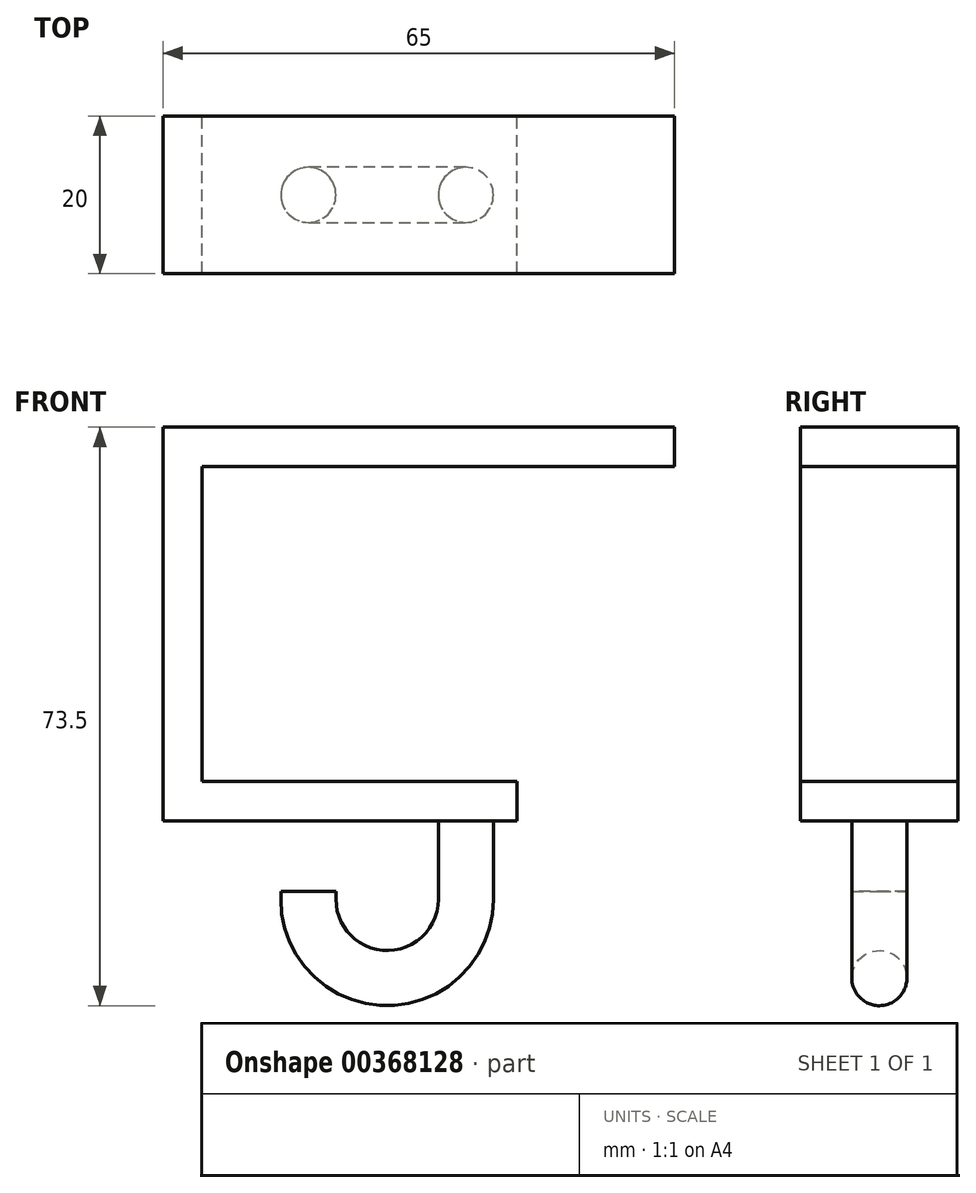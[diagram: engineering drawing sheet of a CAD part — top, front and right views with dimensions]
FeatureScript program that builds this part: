
annotation { "Feature Type Name" : "Feature", "Feature Type Description" : "" }
export const myFeature = defineFeature(function(context is Context, id is Id, definition is map)
    precondition{}
    {
        {
            var Q0;
            Q0=qCreatedBy(makeId("Front.planeOp"),FACE);
            var sketch = newSketch(context, id + "F0", { "sketchPlane" : qUnion([Q0])});
            skLineSegment(sketch, "E0", {"start": v(0, 0) * mm, "end": v(0, -40) * mm});
            skLineSegment(sketch, "E1", {"start": v(0, -40) * mm, "end": v(40, -40) * mm});
            skLineSegment(sketch, "E2", {"start": v(0, 0) * mm, "end": v(60, 0) * mm});
            skLineSegment(sketch, "E3", {"start": v(60, 0) * mm, "end": v(60, 5) * mm});
            skLineSegment(sketch, "E4", {"start": v(60, 5) * mm, "end": v(-5, 5) * mm});
            skLineSegment(sketch, "E5", {"start": v(-5, 5) * mm, "end": v(-5, -45) * mm});
            skLineSegment(sketch, "E6", {"start": v(-5, -45) * mm, "end": v(40, -45) * mm});
            skLineSegment(sketch, "E7", {"start": v(40, -45) * mm, "end": v(40, -40) * mm});
            skSolve(sketch);
        }
        {
            var Q0;
            Q0 = qSketchRegion(id + "F0", true);
            extrude(context, id + "F1", {"entities" : qUnion([Q0]), "depth" : 20 * mm});
        }
        {
            var Q0;
            Q0=makeQuery(id+"F1.opExtrude","SWEPT_FACE",FACE,{"disambiguationData":[OSD([sQuery(id+"F0.wireOp",EDGE,"E6")])]});
            cPlane(context, id + "F2", {"entities" : qUnion([Q0]), "cplaneType" : CPlaneType.OFFSET, "offset" : 0 * mm, "width" : 150 * mm, "height" : 150 * mm});
        }
        {
            var Q0;
            Q0=qCreatedBy(id+"F2.planeOp",FACE);
            var sketch = newSketch(context, id + "F3", { "sketchPlane" : qUnion([Q0])});
            skLineSegment(sketch, "E8.0", {"start": v(40, 20) * mm, "end": v(40, 0) * mm, "construction": true});
            skLineSegment(sketch, "E9.0", {"start": v(-5, 20) * mm, "end": v(40, 20) * mm, "construction": true});
            skLineSegment(sketch, "E10.0", {"start": v(-5, 0) * mm, "end": v(40, 0) * mm, "construction": true});
            skCircle(sketch, "E11", {"center": v(33.47, 10) * mm, "radius": 3.5 * mm});
            skPoint(sketch, "E11.centerSnap0", {"position": v(40, 10) * mm});
            skLineSegment(sketch, "E12.0", {"start": v(-5, 20) * mm, "end": v(-5, 0) * mm, "construction": true});
            skLineSegment(sketch, "E13", {"start": v(-5, 10) * mm, "end": v(40, 10) * mm, "construction": true});
            skSolve(sketch);
        }
        {
            var Q0;
            Q0 = qSketchRegion(id + "F3", true);
            extrude(context, id + "F4", {"entities" : qUnion([Q0]), "operationType" : NewBodyOperationType.ADD, "depth" : 10 * mm});
        }
        {
            var Q0;
            Q0=makeQuery(id+"F4.opExtrude","SWEPT_FACE",FACE,{"disambiguationData":[OSD([sQuery(id+"F3.wireOp",EDGE,"E11")])]});
            cPlane(context, id + "F5", {"entities" : qUnion([Q0]), "cplaneType" : CPlaneType.LINE_ANGLE, "offset" : 25 * mm, "angle" : 90 * degree, "width" : 150 * mm, "height" : 150 * mm});
        }
        {
            var Q0;
            Q0=qCreatedBy(id+"F5.planeOp",FACE);
            var sketch = newSketch(context, id + "F6", { "sketchPlane" : qUnion([Q0])});
            skLineSegment(sketch, "E14.0", {"start": v(-29.97, -55) * mm, "end": v(-36.97, -55) * mm, "construction": true});
            skPoint(sketch, "E15.endSnap0", {"position": v(-33.47, -55) * mm});
            skArc(sketch, "E16", {"start": v(-33.47, -55) * mm, "mid": v(-23.47, -65) * mm, "end": v(-13.47, -55) * mm});
            skSolve(sketch);
        }
        {
            var Q0;
            Q0=makeQuery(id+"F4.opExtrude","CAP_FACE",FACE,{"disambiguationData":[OSD([sQuery(id+"F3.wireOp",EDGE,"E11")])],"isStart":false});
            cPlane(context, id + "F7", {"entities" : qUnion([Q0]), "cplaneType" : CPlaneType.OFFSET, "offset" : 0 * mm, "width" : 150 * mm, "height" : 150 * mm});
        }
        {
            var Q0;
            Q0=qCreatedBy(id+"F7.planeOp",FACE);
            var sketch = newSketch(context, id + "F8", { "sketchPlane" : qUnion([Q0])});
            skCircle(sketch, "E17", {"center": v(13.47, 10) * mm, "radius": 3.5 * mm});
            skSolve(sketch);
        }
        {
            var Q0;
            Q0=makeQuery(id+"F8.imprint","IMPRINT",FACE,{"disambiguationData":[TD([[makeQuery(id+"F8.imprint","IMPRINT",EDGE,{"derivedFrom":sQuery(id+"F8.wireOp",EDGE,"E17")}),1.0]])]});
            var Q1;
            Q1 = qConstructionFilter(qBodyType(qCreatedBy(id + "FfnEyc7QUYgMEDe_1" ,EDGE), BodyType.WIRE), ConstructionObject.NO);
            extrude(context, id + "F9", {"entities" : qUnion([Q0]), "surfaceEntities" : qUnion([Q1]), "oppositeDirection" : true, "depth" : 1 * mm});
        }
        {
            var Q0;
            Q0=makeQuery(id+"F9.opExtrude","CAP_FACE",FACE,{"disambiguationData":[OSD([sQuery(id+"F8.wireOp",EDGE,"E17")])],"isStart":true});
            var Q1;
            Q1=makeQuery(id+"F9.opExtrude","CAP_EDGE",EDGE,{"disambiguationData":[OSD([sQuery(id+"F8.wireOp",EDGE,"E17")])],"isStart":true});
            var Q2;
            Q2=sQuery(id+"F6.wireOp",EDGE,"E16");
            sweep(context, id + "F10", {"operationType" : NewBodyOperationType.ADD, "profiles" : qUnion([Q0]), "surfaceProfiles" : qUnion([Q1]), "path" : qUnion([Q2])});
        }
    });
